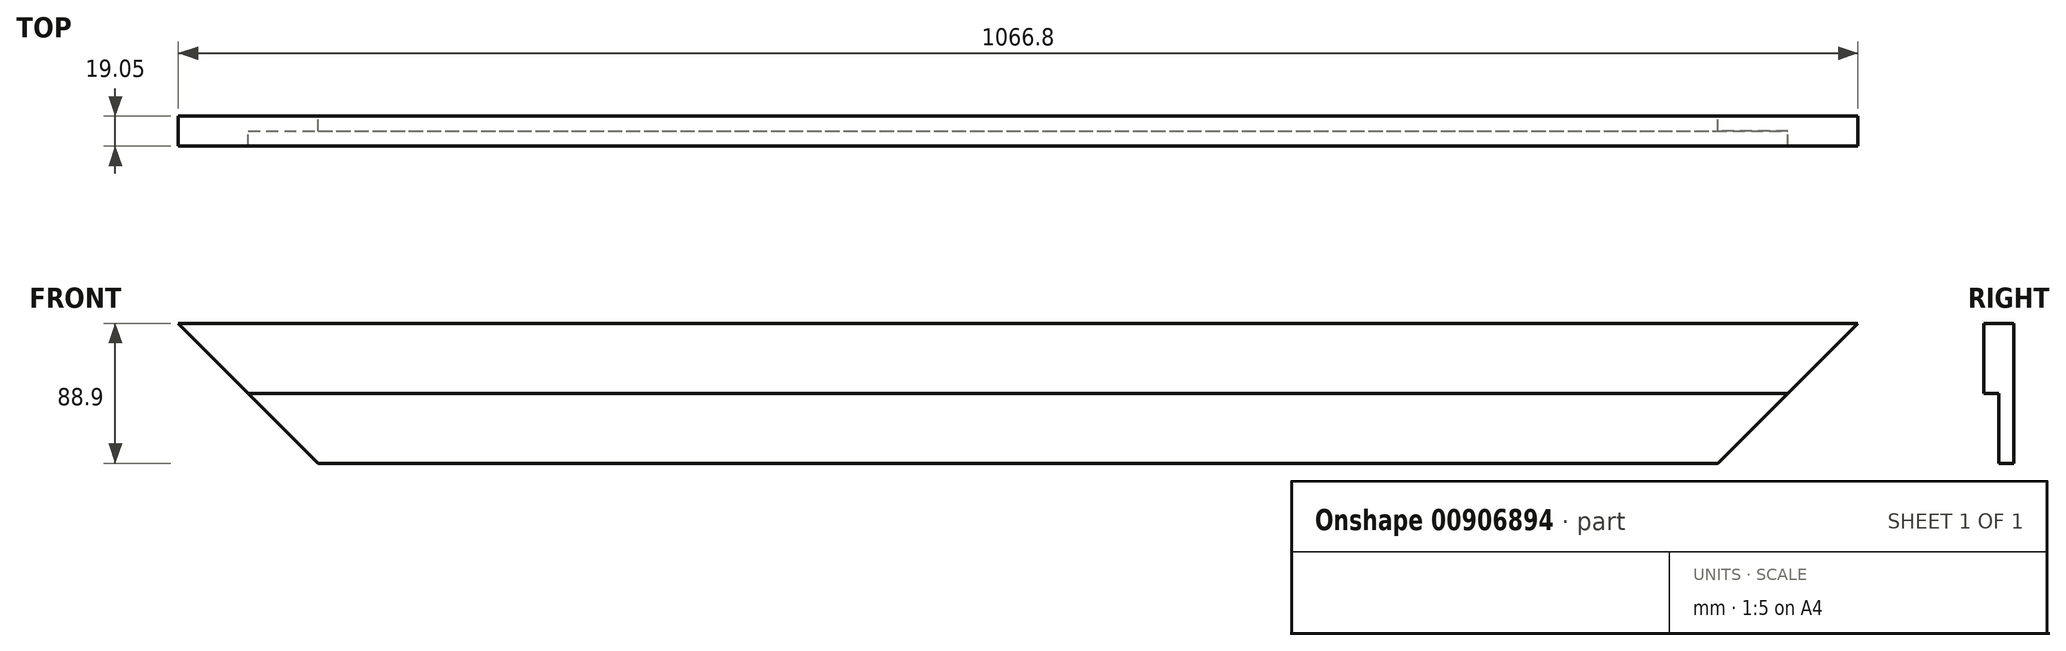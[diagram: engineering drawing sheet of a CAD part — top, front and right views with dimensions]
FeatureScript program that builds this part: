
annotation { "Feature Type Name" : "Feature", "Feature Type Description" : "" }
export const myFeature = defineFeature(function(context is Context, id is Id, definition is map)
    precondition{}
    {
        {
            var Q0;
            Q0=qCreatedBy(makeId("Front.planeOp"),FACE);
            var sketch = newSketch(context, id + "F0", { "sketchPlane" : qUnion([Q0])});
            skLineSegment(sketch, "E0", {"start": v(-533.4, 0) * mm, "end": v(-533.4, 88.9) * mm});
            skLineSegment(sketch, "E1", {"start": v(-533.4, 88.9) * mm, "end": v(533.4, 88.9) * mm});
            skLineSegment(sketch, "E2", {"start": v(533.4, 88.9) * mm, "end": v(533.4, 0) * mm});
            skLineSegment(sketch, "E3", {"start": v(533.4, 0) * mm, "end": v(-533.4, 0) * mm});
            skSolve(sketch);
        }
        {
            var Q0;
            Q0=qSketchRegion(id+"F0",true);
            extrude(context, id + "F1", {"entities" : qUnion([Q0]), "depth" : 19.05 * mm, "offsetDistance" : 25.4 * mm});
        }
        {
            var Q0;
            Q0=makeQuery(id+"F1.opExtrude","SWEPT_FACE",FACE,{"disambiguationData":[OSD([sQuery(id+"F0.wireOp",EDGE,"E2")])]});
            var sketch = newSketch(context, id + "F2", { "sketchPlane" : qUnion([Q0])});
            skLineSegment(sketch, "E4", {"start": v(-9.52, 0) * mm, "end": v(-9.53, 44.45) * mm});
            skLineSegment(sketch, "E5", {"start": v(-19.05, 44.45) * mm, "end": v(-19.05, 0) * mm});
            skLineSegment(sketch, "E6", {"start": v(-19.05, 0) * mm, "end": v(-9.52, 0) * mm});
            skLineSegment(sketch, "E7", {"start": v(-9.53, 44.45) * mm, "end": v(-19.05, 44.45) * mm});
            skSolve(sketch);
        }
        {
            var Q0;
            Q0=qSketchRegion(id+"F2",true);
            extrude(context, id + "F3", {"entities" : qUnion([Q0]), "operationType" : NewBodyOperationType.REMOVE, "endBound" : BoundingType.THROUGH_ALL, "oppositeDirection" : true, "depth" : 25.4 * mm, "offsetDistance" : 25.4 * mm});
        }
        {
            var Q0;
            Q0=makeQuery(id+"F1.opExtrude","CAP_FACE",FACE,{"disambiguationData":[OSD([sQuery(id+"F0.wireOp",EDGE,"E0"),sQuery(id+"F0.wireOp",EDGE,"E1"),sQuery(id+"F0.wireOp",EDGE,"E2"),sQuery(id+"F0.wireOp",EDGE,"E3")])],"isStart":true});
            var sketch = newSketch(context, id + "F4", { "sketchPlane" : qUnion([Q0])});
            skLineSegment(sketch, "E8", {"start": v(0, 0) * mm, "end": v(0, 236.7) * mm, "construction": true});
            skLineSegment(sketch, "E9", {"start": v(-533.4, 88.9) * mm, "end": v(-444.5, 0) * mm});
            skLineSegment(sketch, "E10", {"start": v(-444.5, 0) * mm, "end": v(-533.4, 0) * mm});
            skLineSegment(sketch, "E11", {"start": v(-533.4, 0) * mm, "end": v(-533.4, 88.9) * mm});
            skLineSegment(sketch, "E12.MirrorCS", {"start": v(533.4, 0) * mm, "end": v(533.4, 88.9) * mm});
            skLineSegment(sketch, "E13.MirrorCS", {"start": v(444.5, 0) * mm, "end": v(533.4, 0) * mm});
            skLineSegment(sketch, "E14.MirrorCS", {"start": v(533.4, 88.9) * mm, "end": v(444.5, 0) * mm});
            skSolve(sketch);
        }
        {
            var Q0;
            Q0 = qSketchRegion(id + "F4", true);
            extrude(context, id + "F5", {"entities" : qUnion([Q0]), "operationType" : NewBodyOperationType.REMOVE, "endBound" : BoundingType.THROUGH_ALL, "oppositeDirection" : true, "depth" : 25.4 * mm, "offsetDistance" : 25.4 * mm});
        }
    });
